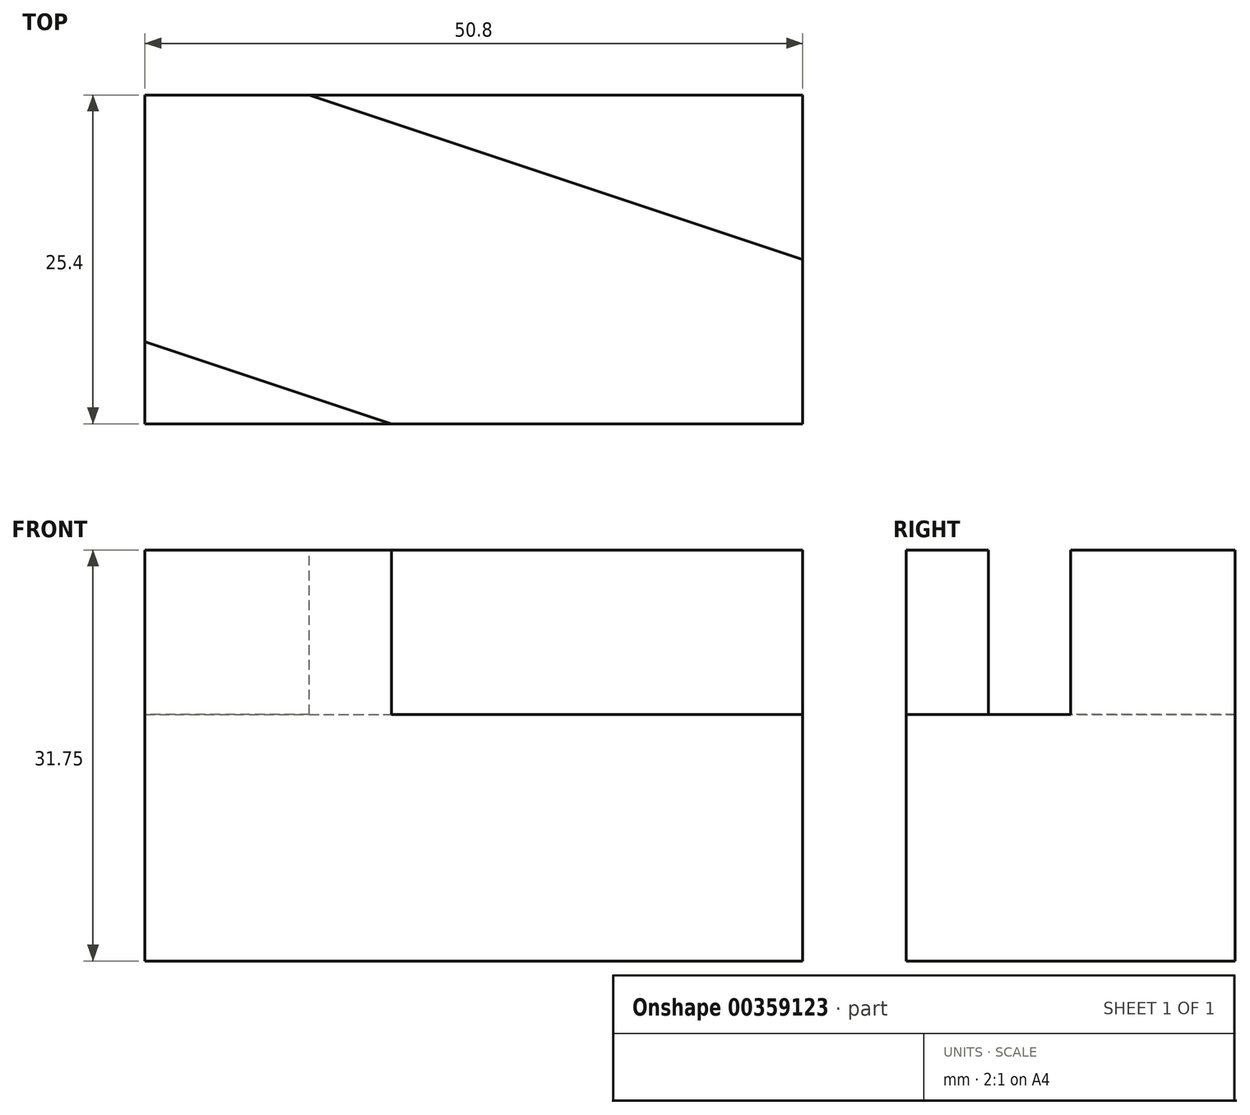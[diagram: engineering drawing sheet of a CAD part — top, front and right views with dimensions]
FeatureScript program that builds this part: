
annotation { "Feature Type Name" : "Feature", "Feature Type Description" : "" }
export const myFeature = defineFeature(function(context is Context, id is Id, definition is map)
    precondition{}
    {
        {
            var Q0;
            Q0=qCreatedBy(makeId("Front.planeOp"),FACE);
            var sketch = newSketch(context, id + "F0", { "sketchPlane" : qUnion([Q0])});
            skLineSegment(sketch, "E0", {"start": v(0, 0) * mm, "end": v(50.8, 0) * mm});
            skLineSegment(sketch, "E1", {"start": v(50.8, 0) * mm, "end": v(50.8, 25.4) * mm});
            skLineSegment(sketch, "E2", {"start": v(50.8, 25.4) * mm, "end": v(0, 25.4) * mm});
            skLineSegment(sketch, "E3", {"start": v(0, 25.4) * mm, "end": v(0, 0) * mm});
            skSolve(sketch);
        }
        {
            var Q0;
            Q0 = qSketchRegion(id + "F0", true);
            extrude(context, id + "F1", {"entities" : qUnion([Q0]), "depth" : 25.4 * mm});
        }
        {
            var Q0;
            Q0=qCreatedBy(makeId("Front.planeOp"),FACE);
            var sketch = newSketch(context, id + "F2", { "sketchPlane" : qUnion([Q0])});
            skSolve(sketch);
        }
        {
            var Q0;
            Q0 = qSketchRegion(id + "F2", true);
            var Q1;
            Q1=makeQuery(id+"F1.opExtrude","SWEPT_FACE",FACE,{"disambiguationData":[OSD([sQuery(id+"F0.wireOp",EDGE,"E2")])]});
            extrude(context, id + "F3", {"entities" : qUnion([Q0, Q1]), "operationType" : NewBodyOperationType.ADD, "depth" : 25.4 * mm});
        }
        {
            var Q0;
            Q0=makeQuery(id+"F3.opExtrude","CAP_FACE",FACE,{"disambiguationData":[OSD([sQuery(id+"F0.wireOp",EDGE,"E2")])],"isStart":false});
            var sketch = newSketch(context, id + "F4", { "sketchPlane" : qUnion([Q0])});
            skLineSegment(sketch, "E4", {"start": v(12.7, 0) * mm, "end": v(50.8, -12.7) * mm});
            skLineSegment(sketch, "E5", {"start": v(0, -19.05) * mm, "end": v(19.05, -25.4) * mm});
            skSolve(sketch);
        }
        {
            var Q0;
            Q0 = qSketchRegion(id + "F4", true);
            var Q1;
            {var subQ8=sQuery(id+"F4.wireOp",EDGE,"E4");Q1=makeQuery(id+"F4.imprint","IMPRINT",FACE,{"disambiguationData":[TD([[makeQuery(id+"F4.imprint","IMPRINT",EDGE,{"derivedFrom":subQ8}),-1.0]])]});}
            extrude(context, id + "F5", {"entities" : qUnion([Q0, Q1]), "operationType" : NewBodyOperationType.REMOVE, "oppositeDirection" : true, "depth" : 12.7 * mm});
        }
        {
            var Q0;
            {var subQ0=sQuery(id+"F0.wireOp",EDGE,"E2");Q0=makeQuery(id+"F3.boolean.opBoolean","MERGE",FACE,{"derivedFrom":[makeQuery(id+"F1.opExtrude","CAP_FACE",FACE,{"disambiguationData":[OSD([sQuery(id+"F0.wireOp",EDGE,"E0"),sQuery(id+"F0.wireOp",EDGE,"E1"),subQ0,sQuery(id+"F0.wireOp",EDGE,"E3")])],"isStart":true}),makeQuery(id+"F3.opExtrude","SWEPT_FACE",FACE,{"disambiguationData":[OSD([subQ0]),TDD([makeQuery(id+"F1.opExtrude","CAP_EDGE",EDGE,{"disambiguationData":[OSD([subQ0])],"isStart":true})])]})]});}
            var sketch = newSketch(context, id + "F6", { "sketchPlane" : qUnion([Q0])});
            skLineSegment(sketch, "E6", {"start": v(0, 19.05) * mm, "end": v(-50.8, 19.05) * mm});
            skSolve(sketch);
        }
        {
            var Q0;
            {var subQ0=sQuery(id+"F6.wireOp",EDGE,"E6");Q0=makeQuery(id+"F6.imprint","IMPRINT",FACE,{"disambiguationData":[TD([[makeQuery(id+"F6.imprint","IMPRINT",EDGE,{"derivedFrom":subQ0}),1.0]])]});}
            extrude(context, id + "F7", {"entities" : qUnion([Q0]), "operationType" : NewBodyOperationType.REMOVE, "oppositeDirection" : true, "depth" : 50.8 * mm});
        }
    });
